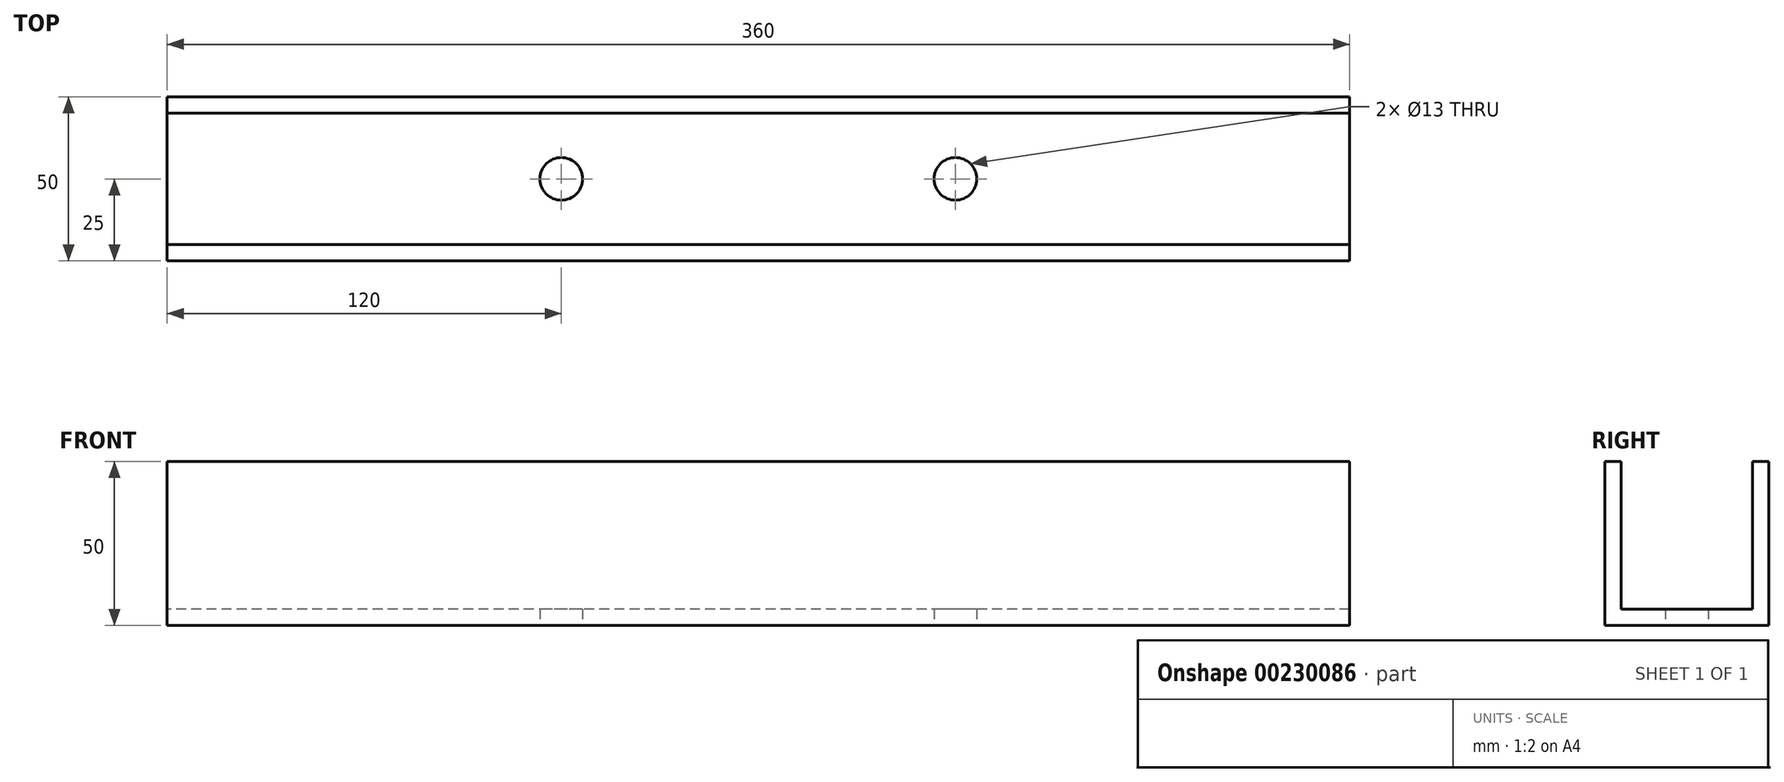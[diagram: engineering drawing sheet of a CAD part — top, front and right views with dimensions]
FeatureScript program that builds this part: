
annotation { "Feature Type Name" : "Feature", "Feature Type Description" : "" }
export const myFeature = defineFeature(function(context is Context, id is Id, definition is map)
    precondition{}
    {
        {
            var Q0;
            Q0=qCreatedBy(makeId("Right.planeOp"),FACE);
            var sketch = newSketch(context, id + "F0", { "sketchPlane" : qUnion([Q0])});
            skLineSegment(sketch, "E0.bottom", {"start": v(0, 0) * mm, "end": v(-50, 0) * mm});
            skLineSegment(sketch, "E0.top", {"start": v(0, 50) * mm, "end": v(-5, 50) * mm});
            skLineSegment(sketch, "E0.left", {"start": v(0, 0) * mm, "end": v(0, 50) * mm});
            skLineSegment(sketch, "E0.right", {"start": v(-50, 0) * mm, "end": v(-50, 50) * mm});
            skLineSegment(sketch, "E1.top", {"start": v(-45, 5) * mm, "end": v(-5, 5) * mm});
            skLineSegment(sketch, "E1.left", {"start": v(-45, 50) * mm, "end": v(-45, 5) * mm});
            skLineSegment(sketch, "E1.right", {"start": v(-5, 50) * mm, "end": v(-5, 5) * mm});
            skLineSegment(sketch, "E2.trimOffspring", {"start": v(-45, 50) * mm, "end": v(-50, 50) * mm});
            skSolve(sketch);
        }
        {
            var Q0;
            Q0 = qSketchRegion(id + "F0", true);
            extrude(context, id + "F1", {"entities" : qUnion([Q0]), "endBound" : BoundingType.SYMMETRIC, "depth" : 360 * mm});
        }
        {
            var Q0;
            Q0=makeQuery(id+"F1.opExtrude","SWEPT_FACE",FACE,{"disambiguationData":[OSD([sQuery(id+"F0.wireOp",EDGE,"E0.bottom")])]});
            var sketch = newSketch(context, id + "F2", { "sketchPlane" : qUnion([Q0])});
            skCircle(sketch, "E3", {"center": v(-60, 25) * mm, "radius": 6.5 * mm});
            skPoint(sketch, "E3.centerSnap0", {"position": v(-180, 25) * mm});
            skCircle(sketch, "E4", {"center": v(60, 25) * mm, "radius": 6.5 * mm});
            skPoint(sketch, "E4.centerSnap0", {"position": v(180, 25) * mm});
            skSolve(sketch);
        }
        {
            var Q0;
            Q0 = qSketchRegion(id + "F2", true);
            extrude(context, id + "F3", {"entities" : qUnion([Q0]), "operationType" : NewBodyOperationType.REMOVE, "oppositeDirection" : true, "depth" : 25 * mm});
        }
    });
